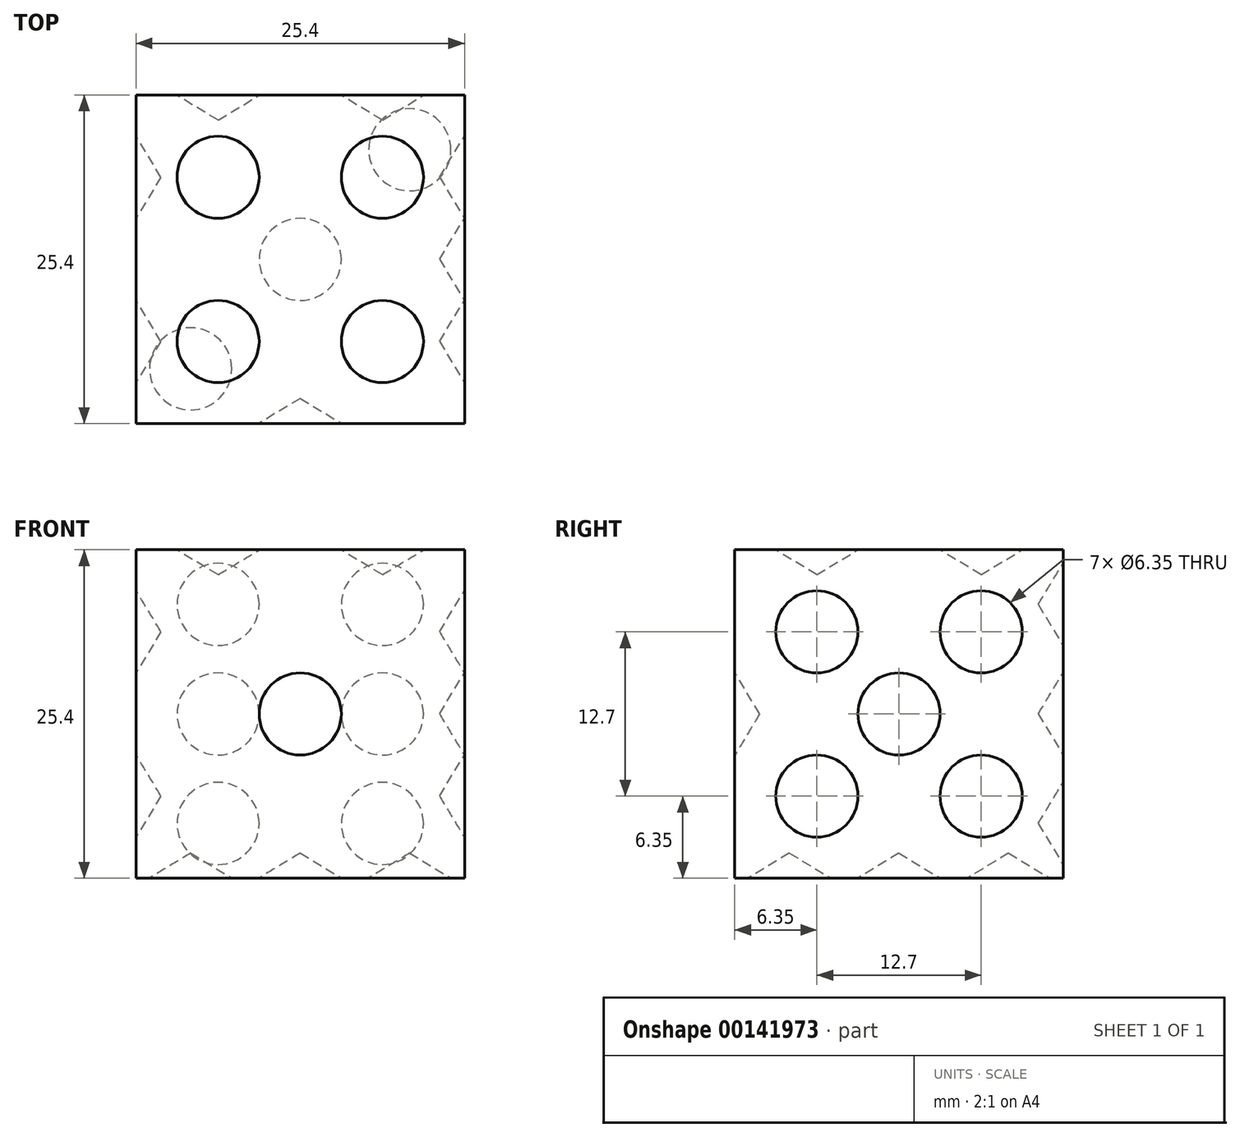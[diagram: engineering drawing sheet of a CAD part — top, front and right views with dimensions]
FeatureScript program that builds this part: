
annotation { "Feature Type Name" : "Feature", "Feature Type Description" : "" }
export const myFeature = defineFeature(function(context is Context, id is Id, definition is map)
    precondition{}
    {
        {
            var Q0;
            Q0=qCreatedBy(makeId("Front.planeOp"),FACE);
            var sketch = newSketch(context, id + "F0", { "sketchPlane" : qUnion([Q0])});
            skLineSegment(sketch, "E0.bottom", {"start": v(0, 0) * mm, "end": v(-25.4, 0) * mm});
            skLineSegment(sketch, "E0.top", {"start": v(0, 25.4) * mm, "end": v(-25.4, 25.4) * mm});
            skLineSegment(sketch, "E0.left", {"start": v(0, 0) * mm, "end": v(0, 25.4) * mm});
            skLineSegment(sketch, "E0.right", {"start": v(-25.4, 0) * mm, "end": v(-25.4, 25.4) * mm});
            skSolve(sketch);
        }
        {
            var Q0;
            Q0=makeQuery(id+"F0.imprint","IMPRINT",FACE,{"disambiguationData":[TD([[makeQuery(id+"F0.imprint","IMPRINT",EDGE,{"derivedFrom":sQuery(id+"F0.wireOp",EDGE,"E0.bottom")}),-1.0]])]});
            extrude(context, id + "F1", {"entities" : qUnion([Q0]), "depth" : 12.7 * mm, "hasSecondDirection" : true, "secondDirectionOppositeDirection" : true, "secondDirectionDepth" : 12.7 * mm});
        }
        {
            var Q0;
            Q0=makeQuery(id+"F1.opExtrude","CAP_FACE",FACE,{"disambiguationData":[OSD([sQuery(id+"F0.wireOp",EDGE,"E0.bottom"),sQuery(id+"F0.wireOp",EDGE,"E0.top"),sQuery(id+"F0.wireOp",EDGE,"E0.left"),sQuery(id+"F0.wireOp",EDGE,"E0.right")])],"isStart":false});
            var sketch = newSketch(context, id + "F2", { "sketchPlane" : qUnion([Q0])});
            skCircle(sketch, "E1", {"center": v(-12.7, 12.7) * mm, "radius": 3.18 * mm});
            skSolve(sketch);
        }
        {
            var Q0;
            Q0=sQuery(id+"F2.wireOp",VERTEX,"E1.center");
            var Q1;
            Q1=makeQuery(id+"F1.opExtrude","SWEPT_BODY",BODY,{"disambiguationData":[OSD([sQuery(id+"F0.wireOp",EDGE,"E0.bottom"),sQuery(id+"F0.wireOp",EDGE,"E0.top"),sQuery(id+"F0.wireOp",EDGE,"E0.left"),sQuery(id+"F0.wireOp",EDGE,"E0.right")])]});
            hole(context, id + "F3", {"style" : HoleStyle.SIMPLE, "endStyle" : HoleEndStyle.BLIND, "holeDiameter" : 6.35 * mm, "holeDepth" : 0.03 * mm, "startFromSketch" : true, "locations" : qUnion([Q0]), "scope" : qUnion([Q1])});
        }
        {
            var Q0;
            Q0=makeQuery(id+"F1.opExtrude","SWEPT_FACE",FACE,{"disambiguationData":[OSD([sQuery(id+"F0.wireOp",EDGE,"E0.top")])]});
            var sketch = newSketch(context, id + "F4", { "sketchPlane" : qUnion([Q0])});
            skLineSegment(sketch, "E2", {"start": v(-25.4, 12.7) * mm, "end": v(-12.7, 12.7) * mm});
            skLineSegment(sketch, "E3", {"start": v(-12.7, 12.7) * mm, "end": v(-12.7, 6.35) * mm});
            skLineSegment(sketch, "E4", {"start": v(-12.7, 6.35) * mm, "end": v(-12.7, 0) * mm});
            skLineSegment(sketch, "E5", {"start": v(-12.7, 0) * mm, "end": v(-12.7, -6.35) * mm});
            skLineSegment(sketch, "E6", {"start": v(-12.7, -6.35) * mm, "end": v(-12.7, -12.7) * mm});
            skLineSegment(sketch, "E7", {"start": v(-12.7, 6.35) * mm, "end": v(-19.05, 6.35) * mm});
            skLineSegment(sketch, "E8", {"start": v(-19.05, 6.35) * mm, "end": v(-25.4, 6.35) * mm});
            skLineSegment(sketch, "E9", {"start": v(-12.7, 6.35) * mm, "end": v(-6.35, 6.35) * mm});
            skLineSegment(sketch, "E10", {"start": v(-6.35, 6.35) * mm, "end": v(0, 6.35) * mm});
            skLineSegment(sketch, "E11", {"start": v(-12.7, -6.35) * mm, "end": v(-6.35, -6.35) * mm});
            skLineSegment(sketch, "E12", {"start": v(-6.35, -6.35) * mm, "end": v(0, -6.35) * mm});
            skLineSegment(sketch, "E13", {"start": v(-12.7, -6.35) * mm, "end": v(-19.05, -6.35) * mm});
            skLineSegment(sketch, "E14", {"start": v(-19.05, -6.35) * mm, "end": v(-25.4, -6.35) * mm});
            skCircle(sketch, "E15", {"center": v(-19.05, 6.35) * mm, "radius": 3.18 * mm});
            skCircle(sketch, "E16", {"center": v(-6.35, 6.35) * mm, "radius": 3.18 * mm});
            skCircle(sketch, "E17", {"center": v(-6.35, -6.35) * mm, "radius": 3.18 * mm});
            skCircle(sketch, "E18", {"center": v(-19.05, -6.35) * mm, "radius": 3.18 * mm});
            skSolve(sketch);
        }
        {
            var Q0;
            Q0=sQuery(id+"F4.wireOp",VERTEX,"E15.center");
            var Q1;
            Q1=sQuery(id+"F4.wireOp",VERTEX,"E9.end");
            var Q2;
            Q2=sQuery(id+"F4.wireOp",VERTEX,"E17.center");
            var Q3;
            Q3=sQuery(id+"F4.wireOp",VERTEX,"E14.start");
            var Q4;
            Q4=makeQuery(id+"F1.opExtrude","SWEPT_BODY",BODY,{"disambiguationData":[OSD([sQuery(id+"F0.wireOp",EDGE,"E0.bottom"),sQuery(id+"F0.wireOp",EDGE,"E0.top"),sQuery(id+"F0.wireOp",EDGE,"E0.left"),sQuery(id+"F0.wireOp",EDGE,"E0.right")])]});
            hole(context, id + "F5", {"style" : HoleStyle.SIMPLE, "endStyle" : HoleEndStyle.BLIND, "holeDiameter" : 6.35 * mm, "holeDepth" : 0.03 * mm, "startFromSketch" : true, "locations" : qUnion([Q0, Q1, Q2, Q3]), "scope" : qUnion([Q4])});
        }
        {
            var Q0;
            Q0=makeQuery(id+"F1.opExtrude","SWEPT_FACE",FACE,{"disambiguationData":[OSD([sQuery(id+"F0.wireOp",EDGE,"E0.bottom")])]});
            var sketch = newSketch(context, id + "F6", { "sketchPlane" : qUnion([Q0])});
            skLineSegment(sketch, "E19", {"start": v(0, -12.7) * mm, "end": v(-4.23, -8.47) * mm});
            skLineSegment(sketch, "E20", {"start": v(-4.23, -8.47) * mm, "end": v(-8.47, -4.23) * mm});
            skLineSegment(sketch, "E21", {"start": v(-8.47, -4.23) * mm, "end": v(-12.7, 0) * mm});
            skLineSegment(sketch, "E22", {"start": v(-12.7, 0) * mm, "end": v(-16.93, 4.23) * mm});
            skLineSegment(sketch, "E23", {"start": v(-16.93, 4.23) * mm, "end": v(-21.17, 8.47) * mm});
            skLineSegment(sketch, "E24", {"start": v(-21.17, 8.47) * mm, "end": v(-25.4, 12.7) * mm});
            skCircle(sketch, "E25", {"center": v(-21.17, 8.47) * mm, "radius": 3.18 * mm});
            skCircle(sketch, "E26", {"center": v(-12.7, 0) * mm, "radius": 3.18 * mm});
            skCircle(sketch, "E27", {"center": v(-4.23, -8.47) * mm, "radius": 3.18 * mm});
            skSolve(sketch);
        }
        {
            var Q0;
            Q0=sQuery(id+"F6.wireOp",VERTEX,"E25.center");
            var Q1;
            Q1=sQuery(id+"F6.wireOp",VERTEX,"E22.start");
            var Q2;
            Q2=sQuery(id+"F6.wireOp",VERTEX,"E20.start");
            var Q3;
            Q3=makeQuery(id+"F1.opExtrude","SWEPT_BODY",BODY,{"disambiguationData":[OSD([sQuery(id+"F0.wireOp",EDGE,"E0.bottom"),sQuery(id+"F0.wireOp",EDGE,"E0.top"),sQuery(id+"F0.wireOp",EDGE,"E0.left"),sQuery(id+"F0.wireOp",EDGE,"E0.right")])]});
            hole(context, id + "F7", {"style" : HoleStyle.SIMPLE, "endStyle" : HoleEndStyle.BLIND, "holeDiameter" : 6.35 * mm, "holeDepth" : 0.03 * mm, "startFromSketch" : true, "locations" : qUnion([Q0, Q1, Q2]), "scope" : qUnion([Q3])});
        }
        {
            var Q0;
            Q0=makeQuery(id+"F1.opExtrude","SWEPT_FACE",FACE,{"disambiguationData":[OSD([sQuery(id+"F0.wireOp",EDGE,"E0.left")])]});
            var sketch = newSketch(context, id + "F8", { "sketchPlane" : qUnion([Q0])});
            skCircle(sketch, "E28", {"center": v(0, 12.7) * mm, "radius": 3.18 * mm});
            skLineSegment(sketch, "E29", {"start": v(12.7, 25.4) * mm, "end": v(6.35, 19.05) * mm});
            skLineSegment(sketch, "E30", {"start": v(6.35, 19.05) * mm, "end": v(0, 12.7) * mm});
            skLineSegment(sketch, "E31", {"start": v(-12.7, 0) * mm, "end": v(-6.35, 6.35) * mm});
            skLineSegment(sketch, "E32", {"start": v(-6.35, 6.35) * mm, "end": v(0, 12.7) * mm});
            skCircle(sketch, "E33", {"center": v(-6.35, 6.35) * mm, "radius": 3.18 * mm});
            skCircle(sketch, "E34", {"center": v(6.35, 19.05) * mm, "radius": 3.18 * mm});
            skCircle(sketch, "E35", {"center": v(6.35, 6.35) * mm, "radius": 3.18 * mm});
            skCircle(sketch, "E36", {"center": v(-6.35, 19.05) * mm, "radius": 3.18 * mm});
            skSolve(sketch);
        }
        {
            var Q0;
            Q0=sQuery(id+"F8.wireOp",VERTEX,"E36.center");
            var Q1;
            Q1=sQuery(id+"F8.wireOp",VERTEX,"E28.center");
            var Q2;
            Q2=sQuery(id+"F8.wireOp",VERTEX,"E34.center");
            var Q3;
            Q3=sQuery(id+"F8.wireOp",VERTEX,"E35.center");
            var Q4;
            Q4=sQuery(id+"F8.wireOp",VERTEX,"E33.center");
            var Q5;
            Q5=makeQuery(id+"F1.opExtrude","SWEPT_BODY",BODY,{"disambiguationData":[OSD([sQuery(id+"F0.wireOp",EDGE,"E0.bottom"),sQuery(id+"F0.wireOp",EDGE,"E0.top"),sQuery(id+"F0.wireOp",EDGE,"E0.left"),sQuery(id+"F0.wireOp",EDGE,"E0.right")])]});
            hole(context, id + "F9", {"style" : HoleStyle.SIMPLE, "endStyle" : HoleEndStyle.BLIND, "holeDiameter" : 6.35 * mm, "holeDepth" : 0.03 * mm, "startFromSketch" : true, "locations" : qUnion([Q0, Q1, Q2, Q3, Q4]), "scope" : qUnion([Q5])});
        }
        {
            var Q0;
            Q0=makeQuery(id+"F1.opExtrude","SWEPT_FACE",FACE,{"disambiguationData":[OSD([sQuery(id+"F0.wireOp",EDGE,"E0.right")])]});
            var sketch = newSketch(context, id + "F10", { "sketchPlane" : qUnion([Q0])});
            skCircle(sketch, "E37", {"center": v(-6.35, 19.05) * mm, "radius": 3.18 * mm});
            skCircle(sketch, "E38", {"center": v(6.35, 6.35) * mm, "radius": 3.18 * mm});
            skSolve(sketch);
        }
        {
            var Q0;
            Q0=sQuery(id+"F10.wireOp",VERTEX,"E37.center");
            var Q1;
            Q1=sQuery(id+"F10.wireOp",VERTEX,"E38.center");
            var Q2;
            Q2=makeQuery(id+"F1.opExtrude","SWEPT_BODY",BODY,{"disambiguationData":[OSD([sQuery(id+"F0.wireOp",EDGE,"E0.bottom"),sQuery(id+"F0.wireOp",EDGE,"E0.top"),sQuery(id+"F0.wireOp",EDGE,"E0.left"),sQuery(id+"F0.wireOp",EDGE,"E0.right")])]});
            hole(context, id + "F11", {"style" : HoleStyle.SIMPLE, "endStyle" : HoleEndStyle.BLIND, "holeDiameter" : 6.35 * mm, "holeDepth" : 0.03 * mm, "startFromSketch" : true, "locations" : qUnion([Q0, Q1]), "scope" : qUnion([Q2])});
        }
        {
            var Q0;
            Q0=makeQuery(id+"F1.opExtrude","CAP_FACE",FACE,{"disambiguationData":[OSD([sQuery(id+"F0.wireOp",EDGE,"E0.bottom"),sQuery(id+"F0.wireOp",EDGE,"E0.top"),sQuery(id+"F0.wireOp",EDGE,"E0.left"),sQuery(id+"F0.wireOp",EDGE,"E0.right")])],"isStart":true});
            var sketch = newSketch(context, id + "F12", { "sketchPlane" : qUnion([Q0])});
            skLineSegment(sketch, "E39", {"start": v(0, 0) * mm, "end": v(6.35, 0) * mm});
            skLineSegment(sketch, "E40", {"start": v(6.35, 0) * mm, "end": v(12.7, 0) * mm});
            skLineSegment(sketch, "E41", {"start": v(12.7, 0) * mm, "end": v(19.05, 0) * mm});
            skLineSegment(sketch, "E42", {"start": v(19.05, 0) * mm, "end": v(25.4, 0) * mm});
            skLineSegment(sketch, "E43", {"start": v(6.35, 0) * mm, "end": v(6.35, 4.23) * mm});
            skLineSegment(sketch, "E44", {"start": v(6.35, 4.23) * mm, "end": v(6.35, 8.47) * mm});
            skLineSegment(sketch, "E45", {"start": v(6.35, 8.47) * mm, "end": v(6.35, 12.7) * mm});
            skLineSegment(sketch, "E46", {"start": v(6.35, 12.7) * mm, "end": v(6.35, 16.93) * mm});
            skLineSegment(sketch, "E47", {"start": v(6.35, 16.93) * mm, "end": v(6.35, 21.17) * mm});
            skLineSegment(sketch, "E48", {"start": v(6.35, 21.17) * mm, "end": v(6.35, 25.4) * mm});
            skCircle(sketch, "E49", {"center": v(6.35, 21.17) * mm, "radius": 3.18 * mm});
            skCircle(sketch, "E50", {"center": v(6.35, 12.7) * mm, "radius": 3.18 * mm});
            skCircle(sketch, "E51", {"center": v(6.35, 4.23) * mm, "radius": 3.18 * mm});
            skLineSegment(sketch, "E52", {"start": v(19.05, 0) * mm, "end": v(19.05, 4.23) * mm});
            skLineSegment(sketch, "E53", {"start": v(19.05, 4.23) * mm, "end": v(19.05, 8.47) * mm});
            skLineSegment(sketch, "E54", {"start": v(19.05, 8.47) * mm, "end": v(19.05, 12.7) * mm});
            skLineSegment(sketch, "E55", {"start": v(19.05, 12.7) * mm, "end": v(19.05, 16.93) * mm});
            skLineSegment(sketch, "E56", {"start": v(19.05, 16.93) * mm, "end": v(19.05, 21.17) * mm});
            skLineSegment(sketch, "E57", {"start": v(19.05, 21.17) * mm, "end": v(19.05, 25.4) * mm});
            skCircle(sketch, "E58", {"center": v(19.05, 21.17) * mm, "radius": 3.18 * mm});
            skCircle(sketch, "E59", {"center": v(19.05, 12.7) * mm, "radius": 3.18 * mm});
            skCircle(sketch, "E60", {"center": v(19.05, 4.23) * mm, "radius": 3.18 * mm});
            skSolve(sketch);
        }
        {
            var Q0;
            Q0=sQuery(id+"F12.wireOp",VERTEX,"E47.end");
            var Q1;
            Q1=sQuery(id+"F12.wireOp",VERTEX,"E50.center");
            var Q2;
            Q2=sQuery(id+"F12.wireOp",VERTEX,"E43.end");
            var Q3;
            Q3=sQuery(id+"F12.wireOp",VERTEX,"E57.start");
            var Q4;
            Q4=sQuery(id+"F12.wireOp",VERTEX,"E55.start");
            var Q5;
            Q5=sQuery(id+"F12.wireOp",VERTEX,"E60.center");
            var Q6;
            Q6=makeQuery(id+"F1.opExtrude","SWEPT_BODY",BODY,{"disambiguationData":[OSD([sQuery(id+"F0.wireOp",EDGE,"E0.bottom"),sQuery(id+"F0.wireOp",EDGE,"E0.top"),sQuery(id+"F0.wireOp",EDGE,"E0.left"),sQuery(id+"F0.wireOp",EDGE,"E0.right")])]});
            hole(context, id + "F13", {"style" : HoleStyle.SIMPLE, "endStyle" : HoleEndStyle.BLIND, "holeDiameter" : 6.35 * mm, "holeDepth" : 0.03 * mm, "startFromSketch" : true, "locations" : qUnion([Q0, Q1, Q2, Q3, Q4, Q5]), "scope" : qUnion([Q6])});
        }
    });
